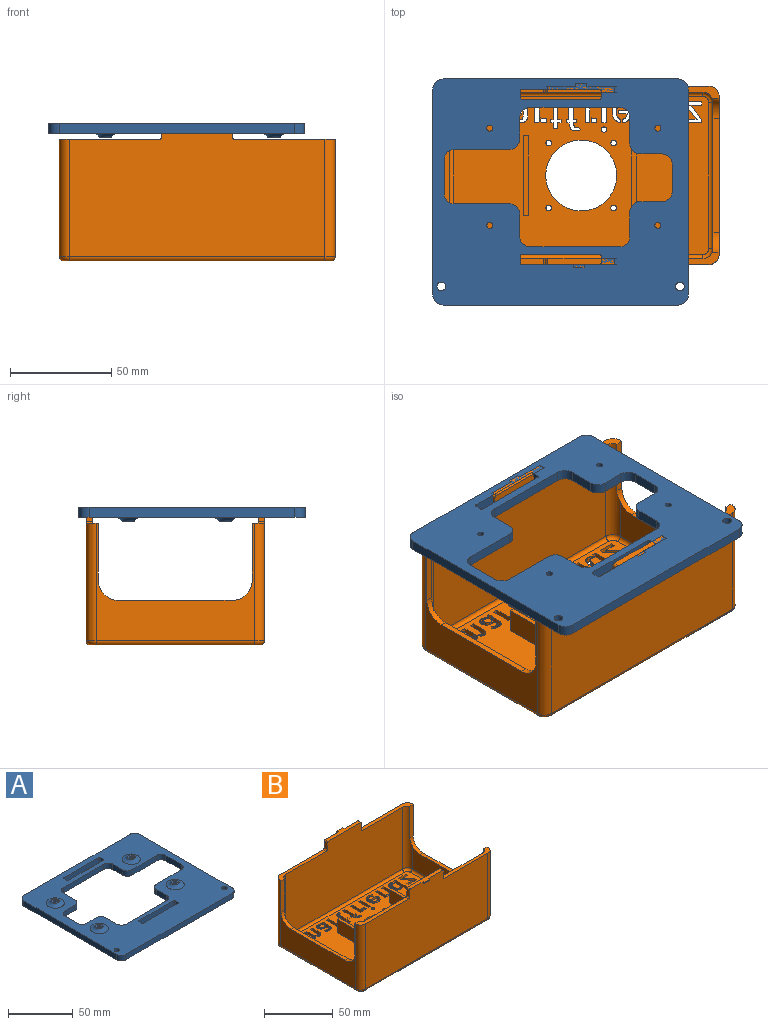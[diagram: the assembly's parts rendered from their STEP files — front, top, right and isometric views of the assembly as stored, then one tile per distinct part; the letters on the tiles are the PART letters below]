
ASSEMBLY  parts=2 mates=1
PART A: 64 faces, bbox 126x111.5x10 mm
  f0: plane 5x3mm, normal (-1,0,0), area 15mm2, adj f18,f19,f22,f27
  f1: plane 38x5mm, normal (0,1,0), area 190mm2, adj f18,f19,f22,f23
  f2: plane 5x3mm, normal (1,0,0), area 15mm2, adj f18,f19,f23,f26
  f3: plane 101.5x5mm, normal (1,0,0), area 507.5mm2, adj f18,f19,f28,f30
  f4: plane 116x5mm, normal (0,1,0), area 580mm2, adj f18,f19,f28,f29
  f5: plane 101.5x5mm, normal (-1,0,0), area 507.5mm2, adj f18,f19,f29,f31
  f6: plane 5x3mm, normal (1,0,0), area 15mm2, adj f18,f19,f20,f25
  f7: plane 38x5mm, normal (0,-1,0), area 190mm2, adj f18,f19,f20,f21
  f8: plane 5x3mm, normal (-1,0,0), area 15mm2, adj f18,f19,f21,f24
  f9: cylinder r=1.5mm len=7mm, axis (0,0,-1), area 66mm2, adj f19,f34
  f10: cylinder r=1.5mm len=7mm, axis (0,0,-1), area 66mm2, adj f19,f33
  f11: cylinder r=1.5mm len=7mm, axis (0,0,-1), area 66mm2, adj f19,f32
  f12: plane 38x5mm, normal (0,-1,0), area 190mm2, adj f18,f19,f26,f27
  f13: cylinder r=2.15mm len=5mm, axis (0,0,-1), area 67.5mm2, adj f18,f19
  f14: cylinder r=2.15mm len=5mm, axis (0,0,-1), area 67.5mm2, adj f18,f19
  f15: plane 116x5mm, normal (0,-1,0), area 580mm2, adj f18,f19,f30,f31
  f16: plane 38x5mm, normal (0,1,0), area 190mm2, adj f18,f19,f24,f25
  f17: cylinder r=1.5mm len=7mm, axis (0,0,-1), area 66mm2, adj f19,f35
  f18: plane 126x111.5mm, normal (0,0,1), area 7777mm2, adj f0,f1,f2,f3,f4,f5,f6,f7
  f19: plane 126x111.5mm, normal (0,0,-1), area 8364.4mm2, adj f0,f1,f2,f3,f4,f5,f6,f7
  f20: cylinder r=1mm len=5mm, axis (0,0,-1), area 7.9mm2, adj f6,f7,f18,f19
  f21: cylinder r=1mm len=5mm, axis (0,0,1), area 7.9mm2, adj f7,f8,f18,f19
  f22: cylinder r=1mm len=5mm, axis (0,0,1), area 7.9mm2, adj f0,f1,f18,f19
  f23: cylinder r=1mm len=5mm, axis (0,0,-1), area 7.9mm2, adj f1,f2,f18,f19
  f24: cylinder r=1mm len=5mm, axis (0,0,-1), area 7.9mm2, adj f8,f16,f18,f19
  f25: cylinder r=1mm len=5mm, axis (0,0,1), area 7.9mm2, adj f6,f16,f18,f19
  f26: cylinder r=1mm len=5mm, axis (0,0,1), area 7.9mm2, adj f2,f12,f18,f19
  f27: cylinder r=1mm len=5mm, axis (0,0,-1), area 7.9mm2, adj f0,f12,f18,f19
  f28: cylinder r=5mm len=5mm, axis (0,0,-1), area 39.3mm2, adj f3,f4,f18,f19
  f29: cylinder r=5mm len=5mm, axis (0,0,1), area 39.3mm2, adj f4,f5,f18,f19
  f30: cylinder r=5mm len=5mm, axis (0,0,1), area 39.3mm2, adj f3,f15,f18,f19
  f31: cylinder r=5mm len=5mm, axis (0,0,-1), area 39.3mm2, adj f5,f15,f18,f19
  f32: plane 6x6mm, normal (0,0,1), area 21.2mm2, adj f11,f39
  f33: plane 6x6mm, normal (0,0,1), area 21.2mm2, adj f10,f38
  f34: plane 6x6mm, normal (0,0,1), area 21.2mm2, adj f9,f37
  f35: plane 6x6mm, normal (0,0,1), area 21.2mm2, adj f17,f36
  f36: torus R=7mm, axis (0,0,1), area 141.1mm2, adj f18,f35
  f37: torus R=7mm, axis (0,0,1), area 141.1mm2, adj f18,f34
  f38: torus R=7mm, axis (0,0,1), area 141.1mm2, adj f18,f33
  f39: torus R=7mm, axis (0,0,1), area 141.1mm2, adj f18,f32
  f40: plane 10.92x5mm, normal (0,1,0), area 54.6mm2, adj f18,f19,f54,f55
  f41: plane 12.23x5mm, normal (1,0,0), area 61.2mm2, adj f18,f19,f55,f62
  f42: plane 44.32x5mm, normal (0,1,0), area 221.6mm2, adj f18,f19,f62,f63
  f43: plane 11.15x5mm, normal (-1,0,0), area 55.7mm2, adj f18,f19,f57,f63
  f44: plane 27.23x5mm, normal (0,1,0), area 136.2mm2, adj f18,f19,f57,f58
  f45: plane 16.9x5mm, normal (-1,0,0), area 84.5mm2, adj f18,f19,f58,f59
  f46: plane 27.23x5mm, normal (0,-1,0), area 136.2mm2, adj f18,f19,f56,f59
  f47: plane 10.72x5mm, normal (-1,0,0), area 53.6mm2, adj f18,f19,f56,f60
  f48: plane 44.32x5mm, normal (0,-1,0), area 221.6mm2, adj f18,f19,f60,f61
  f49: plane 13x5mm, normal (1,0,0), area 65mm2, adj f18,f19,f52,f61
  f50: plane 10.92x5mm, normal (0,-1,0), area 54.6mm2, adj f18,f19,f52,f53
  f51: plane 13.53x5mm, normal (1,0,0), area 67.7mm2, adj f18,f19,f53,f54
  f52: cylinder r=5mm len=5mm, axis (0,0,-1), area 39.3mm2, adj f18,f19,f49,f50
  f53: cylinder r=5mm len=5mm, axis (0,0,1), area 39.3mm2, adj f18,f19,f50,f51
  f54: cylinder r=5mm len=5mm, axis (0,0,-1), area 39.3mm2, adj f18,f19,f40,f51
  f55: cylinder r=5mm len=5mm, axis (0,0,1), area 39.3mm2, adj f18,f19,f40,f41
  f56: cylinder r=5mm len=5mm, axis (0,0,1), area 39.3mm2, adj f18,f19,f46,f47
  f57: cylinder r=5mm len=5mm, axis (0,0,-1), area 39.3mm2, adj f18,f19,f43,f44
  f58: cylinder r=5mm len=5mm, axis (0,0,1), area 39.3mm2, adj f18,f19,f44,f45
  f59: cylinder r=5mm len=5mm, axis (0,0,-1), area 39.3mm2, adj f18,f19,f45,f46
  f60: cylinder r=5mm len=5mm, axis (0,0,-1), area 39.3mm2, adj f18,f19,f47,f48
  f61: cylinder r=5mm len=5mm, axis (0,0,1), area 39.3mm2, adj f18,f19,f48,f49
  f62: cylinder r=5mm len=5mm, axis (0,0,-1), area 39.3mm2, adj f18,f19,f41,f42
  f63: cylinder r=5mm len=5mm, axis (0,0,1), area 39.3mm2, adj f18,f19,f42,f43
PART B: 408 faces, bbox 136.8x91x68 mm
  f0: plane 126x78mm, normal (0,0,1), area 8098mm2, adj f6,f7,f8,f9,f10,f59,f60,f61
  f1: plane 132x84mm, normal (0,0,-1), area 9558.3mm2, adj f6,f7,f8,f9,f10,f51,f52,f53
  f2: plane 49.5x6mm, normal (0,0,1), area 157.2mm2, adj f4,f14,f17,f28,f36,f43,f44
  f3: plane 49.5x6mm, normal (0,0,1), area 157.2mm2, adj f12,f15,f16,f19,f40,f47,f48
  f4: plane 78x58mm, normal (-1,0,0), area 1676.7mm2, adj f2,f5,f24,f25,f26,f27,f28,f44
  f5: plane 49.5x6mm, normal (0,0,1), area 157.2mm2, adj f4,f12,f15,f27,f39,f49,f50
  f6: cylinder r=1.4mm len=3mm, axis (0,0,-1), area 26.4mm2, adj f0,f1
  f7: cylinder r=1.4mm len=3mm, axis (0,0,-1), area 26.4mm2, adj f0,f1
  f8: cylinder r=1.4mm len=3mm, axis (0,0,-1), area 26.4mm2, adj f0,f1
  f9: cylinder r=1.4mm len=3mm, axis (0,0,-1), area 26.4mm2, adj f0,f1
  f10: cylinder r=17.5mm len=35mm, axis (0,0,-1), area 329.9mm2, adj f0,f1
  f11: plane 72x20.97mm, normal (1,0,0), area 1241.2mm2, adj f24,f25,f26,f43,f49,f62
  f12: plane 120x63mm, normal (0,1,0), area 6880mm2, adj f3,f5,f29,f30,f31,f39,f40,f41
  f13: plane 72x20.97mm, normal (-1,0,0), area 1241.2mm2, adj f20,f21,f23,f45,f48,f63
  f14: plane 120x63mm, normal (0,-1,0), area 6880mm2, adj f2,f18,f32,f33,f34,f35,f36,f37
  f15: plane 126x66mm, normal (0,-1,0), area 7579.7mm2, adj f3,f5,f29,f30,f31,f39,f40,f41
  f16: plane 78x58mm, normal (1,0,0), area 1676.7mm2, adj f3,f18,f19,f20,f21,f22,f23,f46
  f17: plane 126x66mm, normal (0,1,0), area 7577.5mm2, adj f2,f18,f32,f33,f34,f35,f36,f37
  f18: plane 49.5x6mm, normal (0,0,1), area 157.2mm2, adj f14,f16,f17,f22,f35,f45,f46
  f19: plane 28.03x3.42mm, normal (0,1,0), area 95.8mm2, adj f3,f16,f23,f48
  f20: plane 56x3mm, normal (0,0,1), area 168mm2, adj f13,f16,f21,f23
  f21: cylinder r=10mm len=10mm, axis (-1,0,0), area 48.5mm2, adj f13,f16,f20,f22,f45
  f22: plane 28.03x3.42mm, normal (0,-1,0), area 95.8mm2, adj f16,f18,f21,f45
  f23: cylinder r=10mm len=10mm, axis (-1,0,0), area 48.5mm2, adj f13,f16,f19,f20,f48
  f24: cylinder r=10mm len=10mm, axis (-1,0,0), area 48.5mm2, adj f4,f11,f26,f27,f49
  f25: cylinder r=10mm len=10mm, axis (-1,0,0), area 48.5mm2, adj f4,f11,f26,f28,f43
  f26: plane 56x3mm, normal (0,0,1), area 168mm2, adj f4,f11,f24,f25
  f27: plane 28.03x3.42mm, normal (0,1,0), area 95.8mm2, adj f4,f5,f24,f49
  f28: plane 28.03x3.42mm, normal (0,-1,0), area 95.8mm2, adj f2,f4,f25,f43
  f29: plane 6x3mm, normal (1,0,0), area 18mm2, adj f12,f15,f40,f42
  f30: plane 6x3mm, normal (-1,0,0), area 18mm2, adj f12,f15,f39,f41
  f31: plane 33x4.5mm, normal (0,0,1), area 106.8mm2, adj f12,f15,f41,f42,f67,f68,f70
  f32: plane 6x3mm, normal (-1,0,0), area 18mm2, adj f14,f17,f36,f38
  f33: plane 6x3mm, normal (1,0,0), area 18mm2, adj f14,f17,f35,f37
  f34: plane 33x4.5mm, normal (0,0,1), area 107.8mm2, adj f14,f17,f37,f38,f71,f72,f74
  f35: cylinder r=1mm len=3mm, axis (0,1,0), area 4.7mm2, adj f14,f17,f18,f33
  f36: cylinder r=1mm len=3mm, axis (0,-1,0), area 4.7mm2, adj f2,f14,f17,f32
  f37: cylinder r=1mm len=3mm, axis (0,-1,0), area 4.7mm2, adj f14,f17,f33,f34
  f38: cylinder r=1mm len=3mm, axis (0,1,0), area 4.7mm2, adj f14,f17,f32,f34
  f39: cylinder r=1mm len=3mm, axis (0,-1,0), area 4.7mm2, adj f5,f12,f15,f30
  f40: cylinder r=1mm len=3mm, axis (0,1,0), area 4.7mm2, adj f3,f12,f15,f29
  f41: cylinder r=1mm len=3mm, axis (0,1,0), area 4.7mm2, adj f12,f15,f30,f31
  f42: cylinder r=1mm len=3mm, axis (0,-1,0), area 4.7mm2, adj f12,f15,f29,f31
  f43: cylinder r=5mm len=55mm, axis (0,0,1), area 366mm2, adj f2,f11,f14,f25,f28,f60
  f44: cylinder r=5mm len=58mm, axis (0,0,-1), area 455.5mm2, adj f2,f4,f17,f56
  f45: cylinder r=5mm len=55mm, axis (0,0,-1), area 366mm2, adj f13,f14,f18,f21,f22,f61
  f46: cylinder r=5mm len=58mm, axis (0,0,1), area 455.5mm2, adj f16,f17,f18,f57
  f47: cylinder r=5mm len=58mm, axis (0,0,-1), area 455.5mm2, adj f3,f15,f16,f53
  f48: cylinder r=5mm len=55mm, axis (0,0,1), area 366mm2, adj f3,f12,f13,f19,f23,f65
  f49: cylinder r=5mm len=55mm, axis (0,0,-1), area 366mm2, adj f5,f11,f12,f24,f27,f64
  f50: cylinder r=5mm len=58mm, axis (0,0,1), area 455.5mm2, adj f4,f5,f15,f52
  f51: cylinder r=2mm len=126mm, axis (1,0,0), area 395.8mm2, adj f1,f15,f52,f53
  f52: torus R=3mm, axis (0,0,1), area 21.1mm2, adj f1,f50,f51,f54
  f53: torus R=3mm, axis (0,0,1), area 21.1mm2, adj f1,f47,f51,f55
  f54: cylinder r=2mm len=78mm, axis (0,-1,0), area 245mm2, adj f1,f4,f52,f56
  f55: cylinder r=2mm len=78mm, axis (0,1,0), area 245mm2, adj f1,f16,f53,f57
  f56: torus R=3mm, axis (0,0,1), area 21.1mm2, adj f1,f44,f54,f58
  f57: torus R=3mm, axis (0,0,1), area 21.1mm2, adj f1,f46,f55,f58
  f58: cylinder r=2mm len=126mm, axis (-1,0,0), area 395.8mm2, adj f1,f17,f56,f57
  f59: cylinder r=2mm len=120mm, axis (1,0,0), area 377mm2, adj f0,f14,f60,f61
  f60: torus R=3mm, axis (0,0,1), area 21.1mm2, adj f0,f43,f59,f62
  f61: torus R=3mm, axis (0,0,1), area 21.1mm2, adj f0,f45,f59,f63
  f62: cylinder r=2mm len=72mm, axis (0,1,0), area 226.2mm2, adj f0,f11,f60,f64
  f63: cylinder r=2mm len=72mm, axis (0,-1,0), area 226.2mm2, adj f0,f13,f61,f65
  f64: torus R=3mm, axis (0,0,1), area 21.1mm2, adj f0,f49,f62,f66
  f65: torus R=3mm, axis (0,0,1), area 21.1mm2, adj f0,f48,f63,f66
  f66: cylinder r=2mm len=120mm, axis (-1,0,0), area 377mm2, adj f0,f12,f64,f65
  f67: plane 1.6x1.5mm, normal (1,0,0), area 1.8mm2, adj f15,f31,f69,f70
  f68: plane 1.6x1.5mm, normal (-1,0,0), area 1.8mm2, adj f15,f31,f69,f70
  f69: plane 5.21x1.5mm, normal (0,-0.5,-0.87), area 9mm2, adj f15,f67,f68,f70
  f70: plane 5.21x0.73mm, normal (0,-1,0), area 3.8mm2, adj f31,f67,f68,f69
  f71: plane 1.8x1.5mm, normal (-1,0,0), area 2.1mm2, adj f17,f34,f73,f74
  f72: plane 1.8x1.5mm, normal (1,0,0), area 2.1mm2, adj f17,f34,f73,f74
  f73: plane 5.85x1.5mm, normal (0,0.5,-0.87), area 10.1mm2, adj f17,f71,f72,f74
  f74: plane 5.85x0.93mm, normal (0,1,0), area 5.5mm2, adj f34,f71,f72,f73
  f75: extruded ~3x1.52mm, area 4.9mm2, adj f0,f1,f76,f88
  f76: extruded ~3x1.47mm, area 5.5mm2, adj f0,f1,f75,f77
  f77: extruded ~3x0.64mm, area 2.1mm2, adj f0,f1,f76,f78
  f78: extruded ~3x0.64mm, area 2mm2, adj f0,f1,f77,f79
  f79: plane 3x1.98mm, normal (-1,0,0), area 5.9mm2, adj f0,f1,f78,f80
  f80: extruded ~3x0.73mm, area 2.6mm2, adj f0,f1,f79,f81
  f81: extruded ~3x0.71mm, area 2.4mm2, adj f0,f1,f80,f82
  f82: extruded ~3x0.83mm, area 2.7mm2, adj f0,f1,f81,f83
  f83: extruded ~3x0.75mm, area 2.6mm2, adj f0,f1,f82,f84
  f84: plane 3x1.85mm, normal (-1,0,0), area 5.6mm2, adj f0,f1,f83,f85
  f85: extruded ~3x1.21mm, area 3.7mm2, adj f0,f1,f84,f86
  f86: extruded ~3x1.05mm, area 3.7mm2, adj f0,f1,f85,f87
  f87: extruded ~3x0.96mm, area 3.6mm2, adj f0,f1,f86,f88
  f88: extruded ~3x1.27mm, area 3.9mm2, adj f0,f1,f75,f87
  f89: plane 3x2.02mm, normal (0,1,0), area 6.1mm2, adj f0,f1,f90,f93
  f90: plane 10.44x3mm, normal (1,0,0), area 31.3mm2, adj f0,f1,f89,f91
  f91: plane 3x2.26mm, normal (0,-1,0), area 6.8mm2, adj f0,f1,f90,f92
  f92: plane 9.37x3mm, normal (-1,0,0), area 28.1mm2, adj f0,f1,f91,f93
  f93: plane 3x1.07mm, normal (-0.98,0.22,0), area 3.3mm2, adj f0,f1,f89,f92
  f94: plane 3x1.96mm, normal (1,0,0), area 5.9mm2, adj f0,f1,f95,f107
  f95: extruded ~3x0.94mm, area 3.2mm2, adj f0,f1,f94,f96
  f96: extruded ~3x0.75mm, area 2.6mm2, adj f0,f1,f95,f97
  f97: extruded ~3x0.77mm, area 2.6mm2, adj f0,f1,f96,f98
  f98: extruded ~3x0.97mm, area 3.2mm2, adj f0,f1,f97,f99
  f99: plane 3x1.76mm, normal (1,0,0), area 5.3mm2, adj f0,f1,f98,f100
  f100: extruded ~3x1.28mm, area 4mm2, adj f0,f1,f99,f101
  f101: extruded ~3x1.03mm, area 3.6mm2, adj f0,f1,f100,f102
  f102: extruded ~3x0.93mm, area 3.5mm2, adj f0,f1,f101,f103
  f103: extruded ~3x1.26mm, area 3.9mm2, adj f0,f1,f102,f104
  f104: extruded ~3x1.23mm, area 3.9mm2, adj f0,f1,f103,f105
  f105: extruded ~3x0.82mm, area 3.4mm2, adj f0,f1,f104,f106
  f106: extruded ~3x1.05mm, area 3.6mm2, adj f0,f1,f105,f107
  f107: extruded ~3x1.13mm, area 3.6mm2, adj f0,f1,f94,f106
  f108: plane 3x1.5mm, normal (0.85,0.53,0), area 5.3mm2, adj f0,f1,f109,f116
  f109: extruded ~3x0.81mm, area 2.8mm2, adj f0,f1,f108,f110
  f110: extruded ~3x0.77mm, area 2.5mm2, adj f0,f1,f109,f111
  f111: extruded ~3x0.77mm, area 2.3mm2, adj f0,f1,f110,f112
  f112: extruded ~3x0.85mm, area 2.6mm2, adj f0,f1,f111,f113
  f113: plane 3x1.72mm, normal (-1,0,0), area 5.2mm2, adj f0,f1,f112,f114
  f114: plane 3x0.09mm, normal (0,1,0), area 0.3mm2, adj f0,f1,f113,f115
  f115: extruded ~3x1.29mm, area 3.9mm2, adj f0,f1,f114,f116
  f116: extruded ~3x0.88mm, area 3mm2, adj f0,f1,f108,f115
  f117: plane 3x1.54mm, normal (-0.9,-0.43,0), area 5.1mm2, adj f0,f1,f118,f122
  f118: extruded ~3x1.37mm, area 4.5mm2, adj f0,f1,f117,f119
  f119: extruded ~3x1.54mm, area 4.7mm2, adj f0,f1,f118,f120
  f120: plane 3x1.83mm, normal (1,0,0), area 5.5mm2, adj f0,f1,f119,f121
  f121: extruded ~3x1.12mm, area 3.4mm2, adj f0,f1,f120,f122
  f122: extruded ~3x1.07mm, area 3.4mm2, adj f0,f1,f117,f121
  f123: extruded ~3x0.96mm, area 2.9mm2, adj f0,f1,f124,f138
  f124: extruded ~3x1.02mm, area 3.4mm2, adj f0,f1,f123,f125
  f125: plane 3x1.46mm, normal (1,0,0), area 4.4mm2, adj f0,f1,f124,f126
  f126: extruded ~3x0.98mm, area 3.1mm2, adj f0,f1,f125,f127
  f127: extruded ~3x0.56mm, area 1.7mm2, adj f0,f1,f126,f128
  f128: extruded ~3x0.77mm, area 2.5mm2, adj f0,f1,f127,f129
  f129: extruded ~3x0.69mm, area 2.4mm2, adj f0,f1,f128,f130
  f130: extruded ~3x1.01mm, area 3.1mm2, adj f0,f1,f129,f131
  f131: extruded ~3x1.19mm, area 3.6mm2, adj f0,f1,f130,f132
  f132: plane 5.69x3mm, normal (1,0,0), area 17.1mm2, adj f0,f1,f131,f133
  f133: plane 3x2.22mm, normal (0,-1,0), area 6.7mm2, adj f0,f1,f132,f134
  f134: plane 7.11x3mm, normal (-1,0,0), area 21.3mm2, adj f0,f1,f133,f135
  f135: extruded ~3x1.38mm, area 4.2mm2, adj f0,f1,f134,f136
  f136: extruded ~3x1.1mm, area 3.9mm2, adj f0,f1,f135,f137
  f137: extruded ~3x0.97mm, area 3.6mm2, adj f0,f1,f136,f138
  f138: extruded ~3x1.18mm, area 3.7mm2, adj f0,f1,f123,f137
  f139: extruded ~3x1.14mm, area 4.7mm2, adj f0,f1,f140,f156
  f140: extruded ~3x1.43mm, area 4.5mm2, adj f0,f1,f139,f141
  f141: extruded ~3x1.01mm, area 3.1mm2, adj f0,f1,f140,f142
  f142: extruded ~3x0.95mm, area 3.1mm2, adj f0,f1,f141,f143
  f143: plane 3x1.46mm, normal (1,0,0), area 4.4mm2, adj f0,f1,f142,f144
  f144: extruded ~3x0.86mm, area 2.7mm2, adj f0,f1,f143,f145
  f145: extruded ~3x0.66mm, area 2mm2, adj f0,f1,f144,f146
  f146: extruded ~3x0.76mm, area 2.5mm2, adj f0,f1,f145,f147
  f147: extruded ~3x0.69mm, area 2.4mm2, adj f0,f1,f146,f148
  f148: extruded ~3x1.01mm, area 3.1mm2, adj f0,f1,f147,f149
  f149: plane 3x1.19mm, normal (1,0,0), area 3.6mm2, adj f0,f1,f148,f150
  f150: plane 5.69x3mm, normal (1,0,0), area 17.1mm2, adj f0,f1,f149,f151
  f151: plane 3x2.24mm, normal (0,-1,0), area 6.7mm2, adj f0,f1,f150,f152
  f152: plane 5.87x3mm, normal (-1,0,0), area 17.6mm2, adj f0,f1,f151,f153
  f153: extruded ~3x0.92mm, area 2.8mm2, adj f0,f1,f152,f154
  f154: extruded ~3x0.84mm, area 2.5mm2, adj f0,f1,f153,f155
  f155: extruded ~3x0.79mm, area 2.4mm2, adj f0,f1,f154,f156
  f156: extruded ~3x0.71mm, area 2.4mm2, adj f0,f1,f139,f155
  f157: plane 3x2.55mm, normal (-1,0,0), area 7.7mm2, adj f0,f1,f158,f191
  f158: extruded ~3x1.31mm, area 3.9mm2, adj f0,f1,f157,f159
  f159: extruded ~3x1.31mm, area 4mm2, adj f0,f1,f158,f160
  f160: extruded ~3x1.08mm, area 3.5mm2, adj f0,f1,f159,f161
  f161: extruded ~3x0.76mm, area 3.1mm2, adj f0,f1,f160,f162
  f162: extruded ~3x0.96mm, area 3.1mm2, adj f0,f1,f161,f163
  f163: extruded ~3x1.08mm, area 3.3mm2, adj f0,f1,f162,f164
  f164: extruded ~3x1.18mm, area 3.5mm2, adj f0,f1,f163,f165
  f165: extruded ~3x1.05mm, area 3.2mm2, adj f0,f1,f164,f166
  f166: extruded ~3x0.85mm, area 2.8mm2, adj f0,f1,f165,f167
  f167: extruded ~3x0.55mm, area 2.1mm2, adj f0,f1,f166,f168
  f168: plane 3x1.28mm, normal (0.84,-0.55,0), area 4.6mm2, adj f0,f1,f167,f169
  f169: extruded ~3x0.34mm, area 1.3mm2, adj f0,f1,f168,f170
  f170: extruded ~3x0.54mm, area 1.9mm2, adj f0,f1,f169,f171
  f171: extruded ~3x0.67mm, area 2.1mm2, adj f0,f1,f170,f172
  f172: extruded ~3x0.77mm, area 2.3mm2, adj f0,f1,f171,f173
  f173: extruded ~3x0.77mm, area 2.3mm2, adj f0,f1,f172,f174
  f174: extruded ~3x0.55mm, area 1.9mm2, adj f0,f1,f173,f175
  f175: extruded ~3x0.79mm, area 2.6mm2, adj f0,f1,f174,f176
  f176: extruded ~3x1.44mm, area 4.3mm2, adj f0,f1,f175,f177
  f177: plane 3.91x3mm, normal (1,0,0), area 11.7mm2, adj f0,f1,f176,f178
  f178: extruded ~3x0.64mm, area 2.7mm2, adj f0,f1,f177,f179
  f179: extruded ~3x0.81mm, area 2.7mm2, adj f0,f1,f178,f180
  f180: plane 3x1.41mm, normal (1,0,0), area 4.2mm2, adj f0,f1,f179,f181
  f181: extruded ~3x1.21mm, area 4mm2, adj f0,f1,f180,f182
  f182: extruded ~3x0.82mm, area 3.4mm2, adj f0,f1,f181,f183
  f183: extruded ~3x0.55mm, area 1.8mm2, adj f0,f1,f182,f184
  f184: extruded ~3x0.45mm, area 1.9mm2, adj f0,f1,f183,f185
  f185: extruded ~3x0.52mm, area 1.8mm2, adj f0,f1,f184,f186
  f186: extruded ~3x0.51mm, area 1.6mm2, adj f0,f1,f185,f187
  f187: plane 3x1.24mm, normal (-0.9,-0.43,0), area 4.1mm2, adj f0,f1,f186,f188
  f188: extruded ~3x0.32mm, area 1.4mm2, adj f0,f1,f187,f189
  f189: extruded ~3x0.54mm, area 1.7mm2, adj f0,f1,f188,f190
  f190: extruded ~3x0.58mm, area 1.8mm2, adj f0,f1,f189,f191
  f191: extruded ~3x0.44mm, area 1.3mm2, adj f0,f1,f157,f190
  f192: extruded ~3x0.97mm, area 3mm2, adj f0,f1,f193,f210
  f193: extruded ~3x0.58mm, area 2.5mm2, adj f0,f1,f192,f194
  f194: extruded ~3x0.76mm, area 2.4mm2, adj f0,f1,f193,f195
  f195: extruded ~3x0.78mm, area 2.3mm2, adj f0,f1,f194,f196
  f196: plane 3x0.41mm, normal (0,-1,0), area 1.2mm2, adj f0,f1,f195,f197
  f197: plane 3x1.32mm, normal (-1,0,0), area 3.9mm2, adj f0,f1,f196,f198
  f198: plane 3x0.81mm, normal (0,1,0), area 2.4mm2, adj f0,f1,f197,f199
  f199: extruded ~3x1.46mm, area 4.4mm2, adj f0,f1,f198,f200
  f200: extruded ~3x1.29mm, area 4.3mm2, adj f0,f1,f199,f201
  f201: extruded ~3x1.02mm, area 4.2mm2, adj f0,f1,f200,f202
  f202: extruded ~3x1.47mm, area 4.6mm2, adj f0,f1,f201,f203
  f203: extruded ~3x1.5mm, area 4.6mm2, adj f0,f1,f202,f204
  f204: extruded ~3x0.98mm, area 3.6mm2, adj f0,f1,f203,f205
  f205: extruded ~3x1.03mm, area 3.5mm2, adj f0,f1,f204,f206
  f206: extruded ~3x1.21mm, area 3.7mm2, adj f0,f1,f205,f207
  f207: extruded ~3x0.24mm, area 0.7mm2, adj f0,f1,f206,f208
  f208: plane 3x1.5mm, normal (-1,0,0), area 4.5mm2, adj f0,f1,f207,f209
  f209: extruded ~3x0.99mm, area 3.4mm2, adj f0,f1,f208,f210
  f210: extruded ~3x1.24mm, area 3.9mm2, adj f0,f1,f192,f209
  f211: plane 3x2mm, normal (0,1,0), area 6mm2, adj f0,f1,f212,f215
  f212: plane 10.44x3mm, normal (1,0,0), area 31.3mm2, adj f0,f1,f211,f213
  f213: plane 3x2.24mm, normal (0,-1,0), area 6.7mm2, adj f0,f1,f212,f214
  f214: plane 9.37x3mm, normal (-1,0,0), area 28.1mm2, adj f0,f1,f213,f215
  f215: plane 3x1.07mm, normal (-0.98,0.22,0), area 3.3mm2, adj f0,f1,f211,f214
  f216: plane 3x1.89mm, normal (1,0,0), area 5.7mm2, adj f0,f1,f217,f222
  f217: extruded ~3x0.79mm, area 2.4mm2, adj f0,f1,f216,f218
  f218: extruded ~3x0.83mm, area 2.5mm2, adj f0,f1,f217,f219
  f219: extruded ~3x1.26mm, area 3.8mm2, adj f0,f1,f218,f220
  f220: plane 3x2.33mm, normal (-1,0,0), area 7mm2, adj f0,f1,f219,f221
  f221: extruded ~3x1.76mm, area 5.3mm2, adj f0,f1,f220,f222
  f222: extruded ~3x1.11mm, area 3.6mm2, adj f0,f1,f216,f221
  f223: plane 5.76x3mm, normal (-1,0,0), area 17.3mm2, adj f0,f1,f224,f247
  f224: plane 3x1.67mm, normal (0,-1,0), area 5mm2, adj f0,f1,f223,f225
  f225: plane 3x1.52mm, normal (-1,0,0), area 4.6mm2, adj f0,f1,f224,f226
  f226: plane 3x1.67mm, normal (0,1,0), area 5mm2, adj f0,f1,f225,f227
  f227: plane 3x2.96mm, normal (-1,0,0), area 8.9mm2, adj f0,f1,f226,f228
  f228: plane 3x2.24mm, normal (0,1,0), area 6.7mm2, adj f0,f1,f227,f229
  f229: plane 3x2.96mm, normal (1,0,0), area 8.9mm2, adj f0,f1,f228,f230
  f230: plane 3x1.37mm, normal (0,1,0), area 4.1mm2, adj f0,f1,f229,f231
  f231: plane 3x1.52mm, normal (1,0,0), area 4.6mm2, adj f0,f1,f230,f232
  f232: plane 3x1.37mm, normal (0,-1,0), area 4.1mm2, adj f0,f1,f231,f233
  f233: plane 5.63x3mm, normal (1,0,0), area 16.9mm2, adj f0,f1,f232,f234
  f234: extruded ~3x0.78mm, area 2.3mm2, adj f0,f1,f233,f235
  f235: extruded ~3x1.03mm, area 3.2mm2, adj f0,f1,f234,f236
  f236: extruded ~3x0.96mm, area 3.3mm2, adj f0,f1,f235,f237
  f237: extruded ~3x0.98mm, area 3.4mm2, adj f0,f1,f236,f238
  f238: extruded ~3x0.49mm, area 1.5mm2, adj f0,f1,f237,f239
  f239: extruded ~3x0.57mm, area 1.7mm2, adj f0,f1,f238,f240
  f240: extruded ~3x0.56mm, area 1.7mm2, adj f0,f1,f239,f241
  f241: extruded ~3x0.49mm, area 1.5mm2, adj f0,f1,f240,f242
  f242: extruded ~3x0.48mm, area 1.5mm2, adj f0,f1,f241,f243
  f243: plane 3x1.37mm, normal (-1,0,0), area 4.1mm2, adj f0,f1,f242,f244
  f244: extruded ~3x0.81mm, area 2.4mm2, adj f0,f1,f243,f245
  f245: extruded ~3x0.69mm, area 2.2mm2, adj f0,f1,f244,f246
  f246: extruded ~3x0.54mm, area 2.2mm2, adj f0,f1,f245,f247
  f247: extruded ~3x0.98mm, area 3mm2, adj f0,f1,f223,f246
  f248: extruded ~3x0.51mm, area 1.5mm2, adj f0,f1,f249,f271
  f249: extruded ~3x0.62mm, area 2mm2, adj f0,f1,f248,f250
  f250: plane 3x1.33mm, normal (-0.88,-0.48,0), area 4.5mm2, adj f0,f1,f249,f251
  f251: extruded ~3x0.41mm, area 1.4mm2, adj f0,f1,f250,f252
  f252: extruded ~3x0.56mm, area 1.8mm2, adj f0,f1,f251,f253
  f253: extruded ~3x0.62mm, area 1.9mm2, adj f0,f1,f252,f254
  f254: extruded ~3x0.59mm, area 1.8mm2, adj f0,f1,f253,f255
  f255: extruded ~3x1.56mm, area 4.8mm2, adj f0,f1,f254,f256
  f256: extruded ~3x0.98mm, area 4mm2, adj f0,f1,f255,f257
  f257: extruded ~3x1.28mm, area 4.2mm2, adj f0,f1,f256,f258
  f258: extruded ~3x1.53mm, area 4.6mm2, adj f0,f1,f257,f259
  f259: plane 3x1.41mm, normal (0,1,0), area 4.2mm2, adj f0,f1,f258,f260
  f260: plane 3x1.52mm, normal (1,0,0), area 4.6mm2, adj f0,f1,f259,f261
  f261: plane 3x1.37mm, normal (0,-1,0), area 4.1mm2, adj f0,f1,f260,f262
  f262: plane 8.93x3mm, normal (1,0,0), area 26.8mm2, adj f0,f1,f261,f263
  f263: plane 3x2.26mm, normal (0,-1,0), area 6.8mm2, adj f0,f1,f262,f264
  f264: plane 8.93x3mm, normal (-1,0,0), area 26.8mm2, adj f0,f1,f263,f265
  f265: plane 3x1.65mm, normal (0,-1,0), area 4.9mm2, adj f0,f1,f264,f266
  f266: plane 3x1.52mm, normal (-1,0,0), area 4.6mm2, adj f0,f1,f265,f267
  f267: plane 3x1.61mm, normal (0,1,0), area 4.8mm2, adj f0,f1,f266,f268
  f268: extruded ~3x0.92mm, area 2.8mm2, adj f0,f1,f267,f269
  f269: extruded ~3x0.77mm, area 2.4mm2, adj f0,f1,f268,f270
  f270: extruded ~3x0.52mm, area 2mm2, adj f0,f1,f269,f271
  f271: extruded ~3x0.62mm, area 2mm2, adj f0,f1,f248,f270
  f272: plane 3x2mm, normal (0,1,0), area 6mm2, adj f0,f1,f273,f276
  f273: plane 10.44x3mm, normal (1,0,0), area 31.3mm2, adj f0,f1,f272,f274
  f274: plane 3x2.24mm, normal (0,-1,0), area 6.7mm2, adj f0,f1,f273,f275
  f275: plane 9.37x3mm, normal (-1,0,0), area 28.1mm2, adj f0,f1,f274,f276
  f276: plane 3x1.07mm, normal (-0.98,0.22,0), area 3.3mm2, adj f0,f1,f272,f275
  f277: plane 3x1.89mm, normal (1,0,0), area 5.7mm2, adj f0,f1,f278,f283
  f278: extruded ~3x0.79mm, area 2.4mm2, adj f0,f1,f277,f279
  f279: extruded ~3x0.83mm, area 2.5mm2, adj f0,f1,f278,f280
  f280: extruded ~3x1.26mm, area 3.8mm2, adj f0,f1,f279,f281
  f281: plane 3x2.33mm, normal (-1,0,0), area 7mm2, adj f0,f1,f280,f282
  f282: extruded ~3x1.76mm, area 5.3mm2, adj f0,f1,f281,f283
  f283: extruded ~3x1.11mm, area 3.6mm2, adj f0,f1,f277,f282
  f284: plane 10.44x3mm, normal (-1,0,0), area 31.3mm2, adj f0,f1,f285,f287
  f285: plane 3x2.26mm, normal (0,1,0), area 6.8mm2, adj f0,f1,f284,f286
  f286: plane 10.44x3mm, normal (1,0,0), area 31.3mm2, adj f0,f1,f285,f287
  f287: plane 3x2.26mm, normal (0,-1,0), area 6.8mm2, adj f0,f1,f284,f286
  f288: extruded ~3x0.95mm, area 3.2mm2, adj f0,f1,f289,f295
  f289: extruded ~3x0.94mm, area 3.1mm2, adj f0,f1,f288,f290
  f290: extruded ~3x0.93mm, area 3.1mm2, adj f0,f1,f289,f291
  f291: extruded ~3x0.95mm, area 3.2mm2, adj f0,f1,f290,f292
  f292: extruded ~3x0.93mm, area 3.1mm2, adj f0,f1,f291,f293
  f293: extruded ~3x0.94mm, area 3.1mm2, adj f0,f1,f292,f294
  f294: extruded ~3x0.94mm, area 3.1mm2, adj f0,f1,f293,f295
  f295: extruded ~3x0.93mm, area 3.1mm2, adj f0,f1,f288,f294
  f296: extruded ~3x1.32mm, area 4.1mm2, adj f0,f1,f297,f319
  f297: extruded ~3x0.92mm, area 3.5mm2, adj f0,f1,f296,f298
  f298: extruded ~3x1.07mm, area 3.6mm2, adj f0,f1,f297,f299
  f299: extruded ~3x1.34mm, area 4.1mm2, adj f0,f1,f298,f300
  f300: extruded ~3x0.98mm, area 3mm2, adj f0,f1,f299,f301
  f301: extruded ~3x1.12mm, area 3.5mm2, adj f0,f1,f300,f302
  f302: extruded ~3x0.97mm, area 3.6mm2, adj f0,f1,f301,f303
  f303: extruded ~3x1.13mm, area 3.8mm2, adj f0,f1,f302,f304
  f304: plane 3x1.78mm, normal (-1,0,0), area 5.3mm2, adj f0,f1,f303,f305
  f305: extruded ~3x1.69mm, area 5.3mm2, adj f0,f1,f304,f306
  f306: extruded ~3x1.38mm, area 5.4mm2, adj f0,f1,f305,f307
  f307: extruded ~3x1.66mm, area 5.7mm2, adj f0,f1,f306,f308
  f308: extruded ~3x2mm, area 6.1mm2, adj f0,f1,f307,f309
  f309: extruded ~3x2.07mm, area 6.4mm2, adj f0,f1,f308,f310
  f310: extruded ~3x1.69mm, area 5.9mm2, adj f0,f1,f309,f311
  f311: extruded ~3x1.52mm, area 5.7mm2, adj f0,f1,f310,f312
  f312: extruded ~3x1.91mm, area 5.9mm2, adj f0,f1,f311,f313
  f313: extruded ~3x2.07mm, area 6.4mm2, adj f0,f1,f312,f314
  f314: extruded ~3x1.43mm, area 5.5mm2, adj f0,f1,f313,f315
  f315: plane 3x1.24mm, normal (-0.84,0.55,0), area 4.5mm2, adj f0,f1,f314,f316
  f316: extruded ~3x0.6mm, area 2.3mm2, adj f0,f1,f315,f317
  f317: extruded ~3x0.69mm, area 2.3mm2, adj f0,f1,f316,f318
  f318: extruded ~3x0.65mm, area 2mm2, adj f0,f1,f317,f319
  f319: extruded ~3x0.51mm, area 1.5mm2, adj f0,f1,f296,f318
  f320: plane 3x1.74mm, normal (1,0,0), area 5.2mm2, adj f0,f1,f321,f332
  f321: extruded ~3x0.91mm, area 2.9mm2, adj f0,f1,f320,f322
  f322: extruded ~3x0.71mm, area 2.9mm2, adj f0,f1,f321,f323
  f323: extruded ~3x0.82mm, area 2.8mm2, adj f0,f1,f322,f324
  f324: extruded ~3x0.93mm, area 2.8mm2, adj f0,f1,f323,f325
  f325: plane 4.28x3mm, normal (0,1,0), area 12.8mm2, adj f0,f1,f324,f326
  f326: plane 3x1.63mm, normal (1,0,0), area 4.9mm2, adj f0,f1,f325,f327
  f327: plane 6.35x3mm, normal (0,-1,0), area 19mm2, adj f0,f1,f326,f328
  f328: extruded ~3x0.89mm, area 2.7mm2, adj f0,f1,f327,f329
  f329: extruded ~3x1.89mm, area 5.8mm2, adj f0,f1,f328,f330
  f330: extruded ~3x1.61mm, area 5.5mm2, adj f0,f1,f329,f331
  f331: extruded ~3x1.38mm, area 5.4mm2, adj f0,f1,f330,f332
  f332: extruded ~3x1.81mm, area 5.7mm2, adj f0,f1,f320,f331
  f333: plane 3x2mm, normal (0,1,0), area 6mm2, adj f0,f1,f334,f337
  f334: plane 10.44x3mm, normal (1,0,0), area 31.3mm2, adj f0,f1,f333,f335
  f335: plane 3x2.24mm, normal (0,-1,0), area 6.7mm2, adj f0,f1,f334,f336
  f336: plane 9.39x3mm, normal (-1,0,0), area 28.2mm2, adj f0,f1,f335,f337
  f337: plane 3x1.05mm, normal (-0.98,0.22,0), area 3.2mm2, adj f0,f1,f333,f336
  f338: extruded ~3x1.15mm, area 4.4mm2, adj f0,f1,f339,f355
  f339: extruded ~3x1.41mm, area 4.4mm2, adj f0,f1,f338,f340
  f340: extruded ~3x1.14mm, area 3.5mm2, adj f0,f1,f339,f341
  f341: extruded ~3x1.08mm, area 3.5mm2, adj f0,f1,f340,f342
  f342: plane 3x1.43mm, normal (1,0,0), area 4.3mm2, adj f0,f1,f341,f343
  f343: extruded ~3x0.84mm, area 2.7mm2, adj f0,f1,f342,f344
  f344: extruded ~3x0.69mm, area 2.1mm2, adj f0,f1,f343,f345
  f345: extruded ~3x0.98mm, area 3.1mm2, adj f0,f1,f344,f346
  f346: extruded ~3x0.69mm, area 2.7mm2, adj f0,f1,f345,f347
  f347: extruded ~3x1.02mm, area 3.2mm2, adj f0,f1,f346,f348
  f348: extruded ~3x1.2mm, area 3.6mm2, adj f0,f1,f347,f349
  f349: plane 5.69x3mm, normal (1,0,0), area 17.1mm2, adj f0,f1,f348,f350
  f350: plane 3x2.26mm, normal (0,-1,0), area 6.8mm2, adj f0,f1,f349,f351
  f351: plane 5.87x3mm, normal (-1,0,0), area 17.6mm2, adj f0,f1,f350,f352
  f352: extruded ~3x0.91mm, area 2.7mm2, adj f0,f1,f351,f353
  f353: extruded ~3x0.92mm, area 2.8mm2, adj f0,f1,f352,f354
  f354: extruded ~3x0.87mm, area 2.7mm2, adj f0,f1,f353,f355
  f355: extruded ~3x0.73mm, area 2.7mm2, adj f0,f1,f338,f354
  f356: plane 3x2.26mm, normal (0,1,0), area 6.8mm2, adj f0,f1,f357,f360
  f357: plane 13.14x3mm, normal (1,0,0), area 39.4mm2, adj f0,f1,f356,f358
  f358: plane 3x1.24mm, normal (0.99,-0.1,0), area 3.7mm2, adj f0,f1,f357,f359
  f359: plane 3x2.13mm, normal (0,-1,0), area 6.4mm2, adj f0,f1,f358,f360
  f360: plane 14.39x3mm, normal (-1,0,0), area 43.2mm2, adj f0,f1,f356,f359
  f361: extruded ~3x2.34mm, area 7.1mm2, adj f0,f1,f362,f385
  f362: extruded ~3x1.97mm, area 6.7mm2, adj f0,f1,f361,f363
  f363: extruded ~3x1.27mm, area 4.7mm2, adj f0,f1,f362,f364
  f364: extruded ~3x1.45mm, area 4.5mm2, adj f0,f1,f363,f365
  f365: extruded ~3x1.23mm, area 3.7mm2, adj f0,f1,f364,f366
  f366: extruded ~3x1.03mm, area 3.3mm2, adj f0,f1,f365,f367
  f367: plane 3x1.93mm, normal (-1,0,0), area 5.8mm2, adj f0,f1,f366,f368
  f368: extruded ~3x1.53mm, area 5.3mm2, adj f0,f1,f367,f369
  f369: extruded ~3x0.99mm, area 3.1mm2, adj f0,f1,f368,f370
  f370: extruded ~3x0.77mm, area 3.3mm2, adj f0,f1,f369,f371
  f371: extruded ~3x1.12mm, area 3.7mm2, adj f0,f1,f370,f372
  f372: extruded ~3x1.38mm, area 4.2mm2, adj f0,f1,f371,f373
  f373: extruded ~3x1.39mm, area 4.2mm2, adj f0,f1,f372,f374
  f374: extruded ~3x1.15mm, area 3.7mm2, adj f0,f1,f373,f375
  f375: extruded ~3x0.79mm, area 3.3mm2, adj f0,f1,f374,f376
  f376: extruded ~3x1.02mm, area 3.2mm2, adj f0,f1,f375,f377
  f377: extruded ~3x0.87mm, area 2.7mm2, adj f0,f1,f376,f378
  f378: extruded ~3x0.7mm, area 2.7mm2, adj f0,f1,f377,f379
  f379: plane 3x1.96mm, normal (-1,0,0), area 5.9mm2, adj f0,f1,f378,f380
  f380: extruded ~3x0.92mm, area 3mm2, adj f0,f1,f379,f381
  f381: extruded ~3x1.09mm, area 3.3mm2, adj f0,f1,f380,f382
  f382: extruded ~3x1.51mm, area 4.6mm2, adj f0,f1,f381,f383
  f383: extruded ~3x1.4mm, area 5mm2, adj f0,f1,f382,f384
  f384: extruded ~3x1.59mm, area 5.7mm2, adj f0,f1,f383,f385
  f385: extruded ~3x2.42mm, area 7.4mm2, adj f0,f1,f361,f384
  f386: plane 3x1.8mm, normal (1,0,0), area 5.4mm2, adj f0,f1,f387,f397
  f387: plane 5.74x3mm, normal (0,-1,0), area 17.2mm2, adj f0,f1,f386,f388
  f388: plane 3x0.37mm, normal (0.62,0.78,0), area 1.4mm2, adj f0,f1,f387,f389
  f389: plane 6.56x5.37mm, normal (0.77,0.63,0), area 25.4mm2, adj f0,f1,f388,f390
  f390: plane 3x1.8mm, normal (1,0,0), area 5.4mm2, adj f0,f1,f389,f391
  f391: plane 7.94x3mm, normal (0,-1,0), area 23.8mm2, adj f0,f1,f390,f392
  f392: plane 3x1.8mm, normal (-1,0,0), area 5.4mm2, adj f0,f1,f391,f393
  f393: plane 5.74x3mm, normal (0,1,0), area 17.2mm2, adj f0,f1,f392,f394
  f394: plane 3x0.37mm, normal (-0.62,-0.78,0), area 1.4mm2, adj f0,f1,f393,f395
  f395: plane 6.56x5.37mm, normal (-0.77,-0.63,0), area 25.4mm2, adj f0,f1,f394,f396
  f396: plane 3x1.8mm, normal (-1,0,0), area 5.4mm2, adj f0,f1,f395,f397
  f397: plane 7.94x3mm, normal (0,1,0), area 23.8mm2, adj f0,f1,f386,f396
  f398: plane 39.28x12mm, normal (-1,0,0), area 471.3mm2, adj f0,f399,f401,f402
  f399: plane 12x2.52mm, normal (0,-1,0), area 30.3mm2, adj f0,f398,f400,f402
  f400: plane 39.28x12mm, normal (1,0,0), area 471.3mm2, adj f0,f399,f401,f402
  f401: plane 12x2.52mm, normal (0,1,0), area 30.3mm2, adj f0,f398,f400,f402
  f402: plane 39.28x2.52mm, normal (0,0,1), area 99.1mm2, adj f398,f399,f400,f401
  f403: plane 39.28x12mm, normal (-1,0,0), area 471.3mm2, adj f0,f404,f406,f407
  f404: plane 12x2.58mm, normal (0,-1,0), area 30.9mm2, adj f0,f403,f405,f407
  f405: plane 39.28x12mm, normal (1,0,0), area 471.3mm2, adj f0,f404,f406,f407
  f406: plane 12x2.58mm, normal (0,1,0), area 30.9mm2, adj f0,f403,f405,f407
  f407: plane 39.28x2.58mm, normal (0,0,1), area 101.2mm2, adj f403,f404,f405,f406
PLACE A rot(axis=(0,1,0),180deg) t=(87.47,27.8,99.47)mm
PLACE B t=(79.76,43.8,31.47)mm
MATE fastened A.f19 <-> B.f31  axis (0,0,1) through (74.22,47.8,99.47)mm
